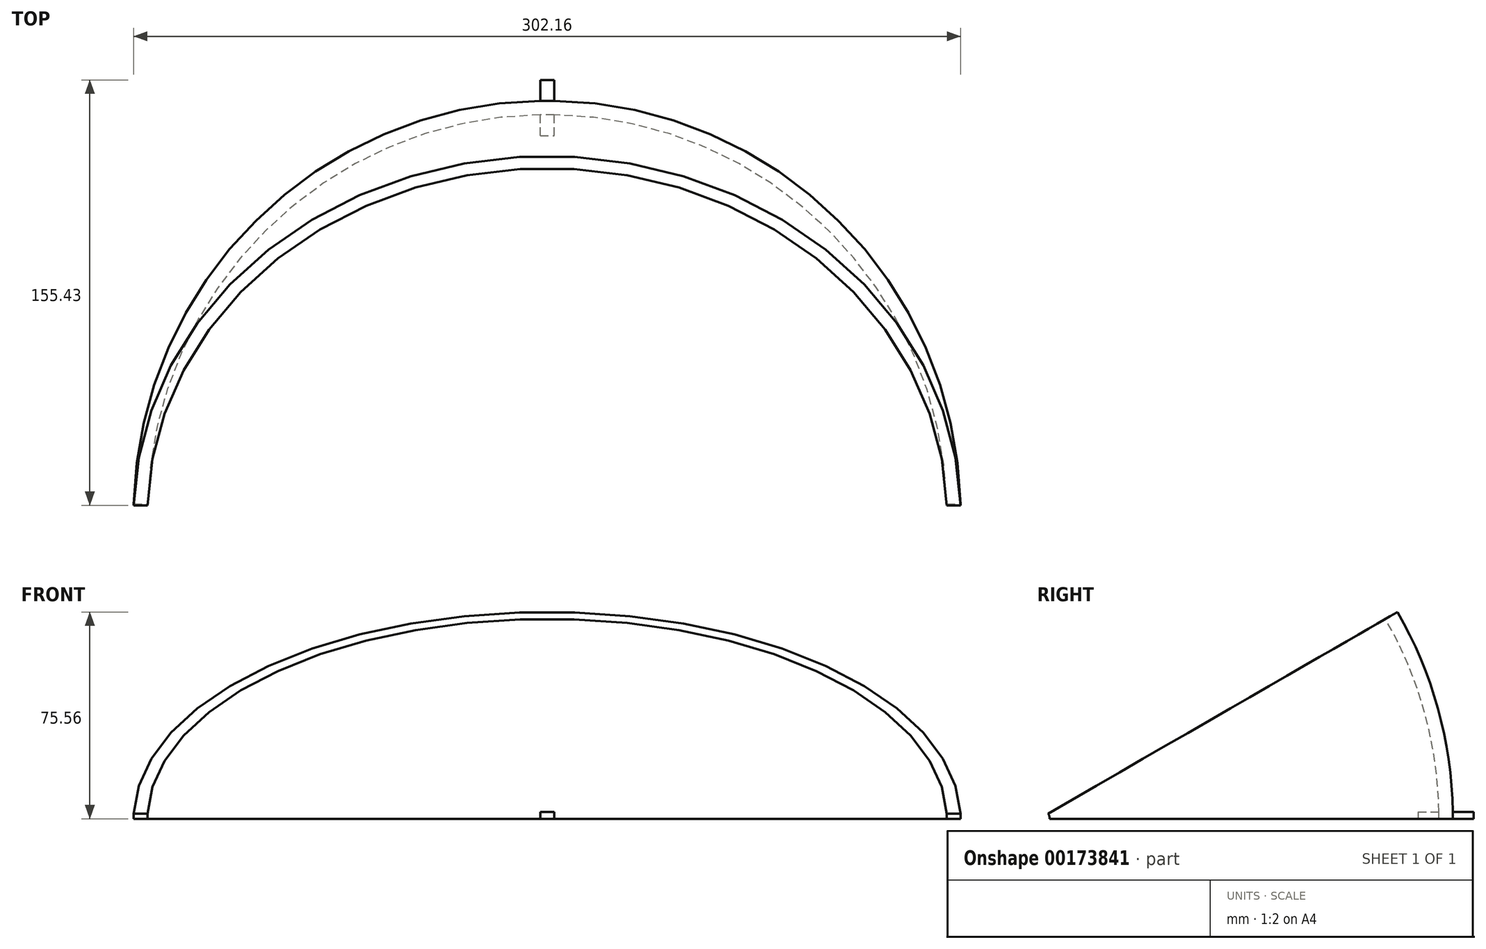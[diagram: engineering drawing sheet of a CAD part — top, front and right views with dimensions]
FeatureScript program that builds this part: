
annotation { "Feature Type Name" : "Feature", "Feature Type Description" : "" }
export const myFeature = defineFeature(function(context is Context, id is Id, definition is map)
    precondition{}
    {
        {
            var Q0;
            Q0=qCreatedBy(makeId("Top.planeOp"),FACE);
            var sketch = newSketch(context, id + "F0", { "sketchPlane" : qUnion([Q0])});
            skLineSegment(sketch, "E0", {"start": v(0, 0) * mm, "end": v(-146.05, 0) * mm, "construction": true});
            skArc(sketch, "E1", {"start": v(-146.05, 0) * mm, "mid": v(0, 146.05) * mm, "end": v(146.05, 0) * mm});
            skLineSegment(sketch, "E2", {"start": v(-146.05, 0) * mm, "end": v(-151.13, 0) * mm});
            skArc(sketch, "E3", {"start": v(-151.13, 0) * mm, "mid": v(0, 151.13) * mm, "end": v(151.13, 0) * mm});
            skLineSegment(sketch, "E4", {"start": v(146.05, 0) * mm, "end": v(151.13, 0) * mm});
            skSolve(sketch);
        }
        {
            var Q0;
            Q0=qSketchRegion(id+"F0",true);
            var Q1;
            Q1=sQuery(id+"F0.wireOp",EDGE,"E0");
            revolve(context, id + "F1", {"entities" : qUnion([Q0]), "axis" : qUnion([Q1]), "revolveType" : RevolveType.ONE_DIRECTION, "oppositeDirection" : true, "angle" : 30 * degree});
        }
        {
            var Q0;
            Q0=qCreatedBy(makeId("Right.planeOp"),FACE);
            var sketch = newSketch(context, id + "F2", { "sketchPlane" : qUnion([Q0])});
            skCircle(sketch, "E5", {"center": v(0, 0) * mm, "radius": 3.81 * mm});
            skSolve(sketch);
        }
        {
            var Q0;
            Q0=qSketchRegion(id+"F2",true);
            extrude(context, id + "F3", {"entities" : qUnion([Q0]), "operationType" : NewBodyOperationType.REMOVE, "endBound" : BoundingType.THROUGH_ALL, "oppositeDirection" : true, "depth" : 25.4 * mm, "hasSecondDirection" : true, "secondDirectionBound" : SecondDirectionBoundingType.THROUGH_ALL, "secondDirectionOppositeDirection" : false, "secondDirectionDepth" : 25.4 * mm});
        }
        {
            var Q0;
            Q0=qCreatedBy(makeId("Top.planeOp"),FACE);
            var sketch = newSketch(context, id + "F4", { "sketchPlane" : qUnion([Q0])});
            skLineSegment(sketch, "E6", {"start": v(0, 0) * mm, "end": v(2.54, 0) * mm, "construction": true});
            skLineSegment(sketch, "E7", {"start": v(0, 0) * mm, "end": v(-2.54, 0) * mm, "construction": true});
            skLineSegment(sketch, "E8", {"start": v(0, 0) * mm, "end": v(-146.05, 0) * mm, "construction": true});
            skLineSegment(sketch, "E9", {"start": v(0, 0) * mm, "end": v(-151.13, 0) * mm, "construction": true});
            skArc(sketch, "E10", {"start": v(-151.13, 0) * mm, "mid": v(0, 151.13) * mm, "end": v(151.13, 0) * mm, "construction": true});
            skArc(sketch, "E11", {"start": v(-146.05, 0) * mm, "mid": v(0, 146.05) * mm, "end": v(146.05, 0) * mm, "construction": true});
            skLineSegment(sketch, "E12", {"start": v(2.54, 0) * mm, "end": v(2.54, 151.1) * mm, "construction": true});
            skLineSegment(sketch, "E13", {"start": v(2.54, 151.1) * mm, "end": v(2.54, 158.73) * mm, "construction": true});
            skLineSegment(sketch, "E14", {"start": v(-2.54, 0) * mm, "end": v(-2.54, 146.03) * mm, "construction": true});
            skLineSegment(sketch, "E15", {"start": v(-2.54, 146.03) * mm, "end": v(-2.54, 138.4) * mm, "construction": true});
            skLineSegment(sketch, "E16.bottom", {"start": v(-2.54, 138.4) * mm, "end": v(2.54, 138.4) * mm});
            skLineSegment(sketch, "E16.top", {"start": v(-2.54, 158.73) * mm, "end": v(2.54, 158.73) * mm});
            skLineSegment(sketch, "E16.left", {"start": v(-2.54, 138.4) * mm, "end": v(-2.54, 158.73) * mm});
            skLineSegment(sketch, "E16.right", {"start": v(2.54, 138.4) * mm, "end": v(2.54, 158.73) * mm});
            skSolve(sketch);
        }
        {
            var Q0;
            Q0 = qSketchRegion(id + "F4", true);
            extrude(context, id + "F5", {"entities" : qUnion([Q0]), "operationType" : NewBodyOperationType.ADD, "depth" : 2.54 * mm});
        }
    });
